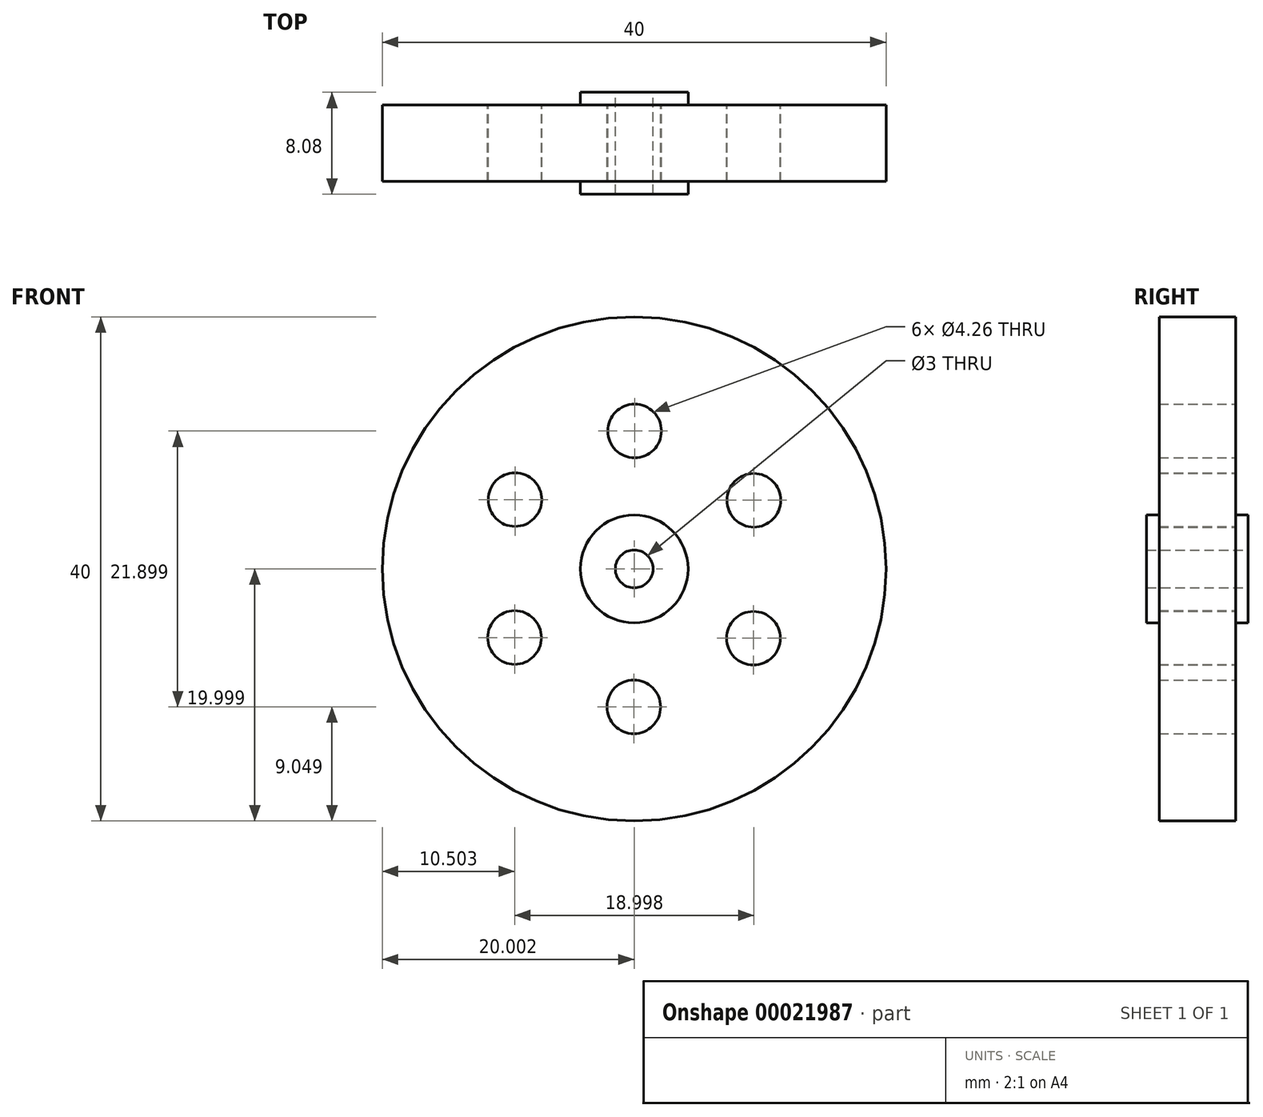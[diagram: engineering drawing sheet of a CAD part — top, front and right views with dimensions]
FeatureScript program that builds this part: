
annotation { "Feature Type Name" : "Feature", "Feature Type Description" : "" }
export const myFeature = defineFeature(function(context is Context, id is Id, definition is map)
    precondition{}
    {
        {
            var Q0;
            Q0=qCreatedBy(makeId("Front.planeOp"),FACE);
            var sketch = newSketch(context, id + "F0", { "sketchPlane" : qUnion([Q0])});
            skCircle(sketch, "E0", {"center": v(-0.3, 0.15) * mm, "radius": 20 * mm});
            skCircle(sketch, "E1", {"center": v(-0.27, 11.1) * mm, "radius": 2.13 * mm});
            skCircle(sketch, "E2.1.0", {"center": v(-9.76, 5.65) * mm, "radius": 2.13 * mm});
            skCircle(sketch, "E2.2.0", {"center": v(-9.8, -5.3) * mm, "radius": 2.13 * mm});
            skCircle(sketch, "E2.3.0", {"center": v(-0.33, -10.8) * mm, "radius": 2.13 * mm});
            skCircle(sketch, "E2.4.0", {"center": v(9.17, -5.35) * mm, "radius": 2.13 * mm});
            skCircle(sketch, "E2.5.0", {"center": v(9.2, 5.6) * mm, "radius": 2.13 * mm});
            skCircle(sketch, "E3", {"center": v(-0.3, 0.15) * mm, "radius": 4.28 * mm});
            skCircle(sketch, "E4", {"center": v(-0.3, 0.15) * mm, "radius": 1.5 * mm});
            skSolve(sketch);
        }
        {
            var Q0;
            Q0=makeQuery(id+"F0.imprint","IMPRINT",FACE,{"disambiguationData":[TD([[makeQuery(id+"F0.imprint","IMPRINT",EDGE,{"derivedFrom":sQuery(id+"F0.wireOp",EDGE,"E0")}),1.0]])]});
            extrude(context, id + "F1", {"entities" : qUnion([Q0]), "endBound" : BoundingType.SYMMETRIC, "depth" : 6.06 * mm});
        }
        {
            var Q0;
            Q0=makeQuery(id+"F0.imprint","IMPRINT",FACE,{"disambiguationData":[TD([[makeQuery(id+"F0.imprint","IMPRINT",EDGE,{"derivedFrom":sQuery(id+"F0.wireOp",EDGE,"E3")}),1.0]])]});
            extrude(context, id + "F2", {"entities" : qUnion([Q0]), "operationType" : NewBodyOperationType.ADD, "endBound" : BoundingType.SYMMETRIC, "depth" : 8.08 * mm});
        }
    });
